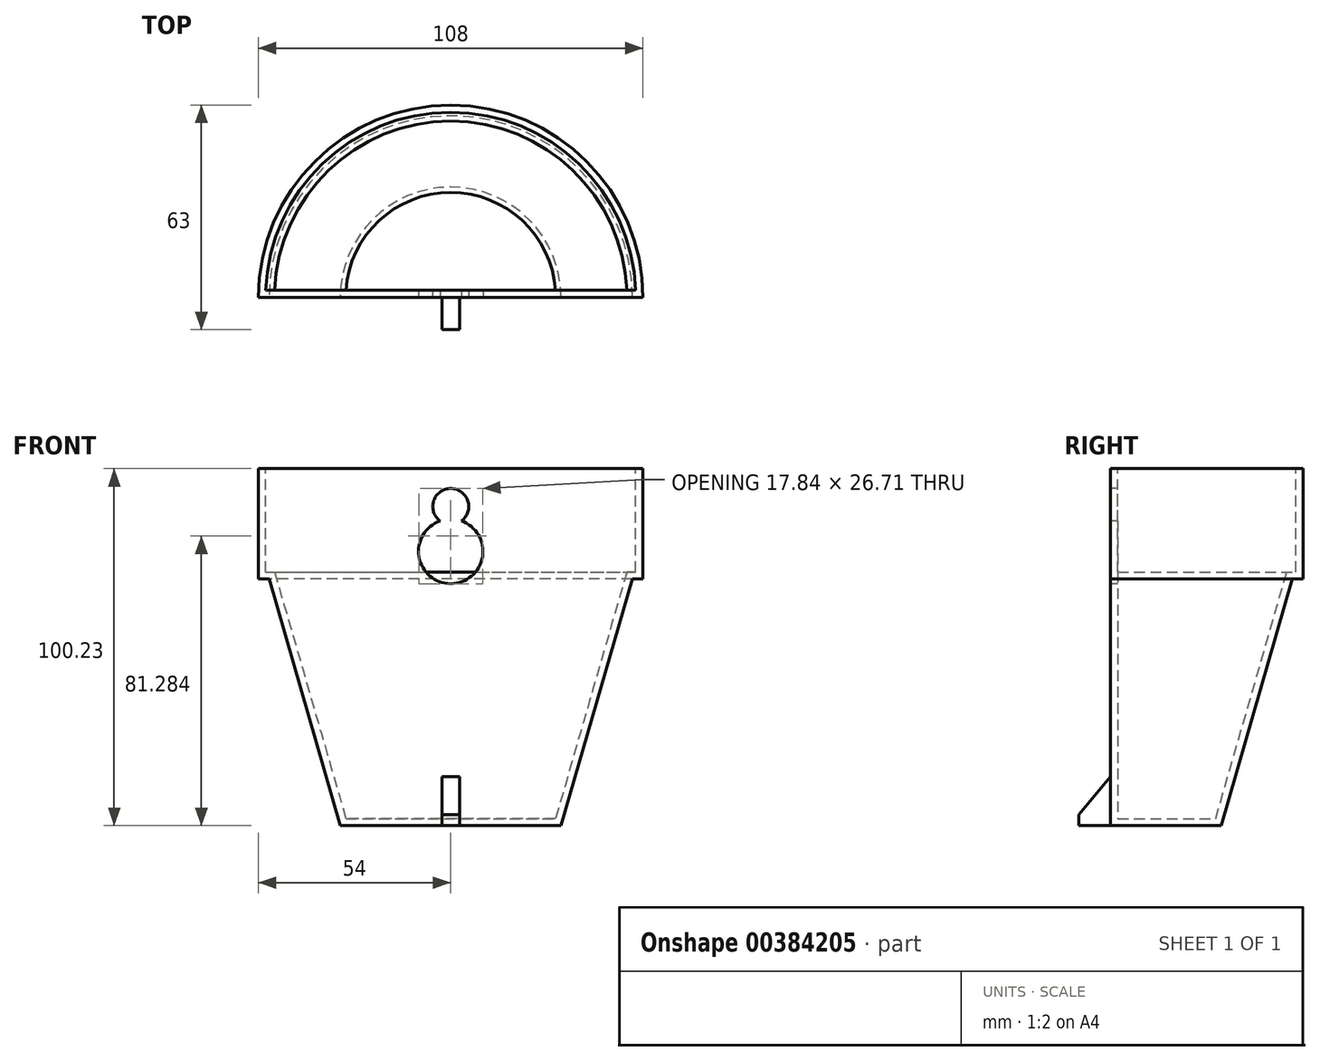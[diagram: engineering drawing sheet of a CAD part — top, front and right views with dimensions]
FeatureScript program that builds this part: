
annotation { "Feature Type Name" : "Feature", "Feature Type Description" : "" }
export const myFeature = defineFeature(function(context is Context, id is Id, definition is map)
    precondition{}
    {
        {
            var Q0;
            Q0=qCreatedBy(makeId("Front.planeOp"),FACE);
            var sketch = newSketch(context, id + "F0", { "sketchPlane" : qUnion([Q0])});
            skLineSegment(sketch, "E0", {"start": v(0, 49.42) * mm, "end": v(-54, 49.42) * mm});
            skLineSegment(sketch, "E1", {"start": v(-54, 49.42) * mm, "end": v(-54, 18.42) * mm});
            skLineSegment(sketch, "E2", {"start": v(0, -50.8) * mm, "end": v(-31, -50.8) * mm});
            skLineSegment(sketch, "E3", {"start": v(-54, 18.42) * mm, "end": v(-51, 18.42) * mm});
            skLineSegment(sketch, "E4", {"start": v(0, 49.42) * mm, "end": v(0, -50.8) * mm});
            skLineSegment(sketch, "E5", {"start": v(-51, 18.42) * mm, "end": v(-31, -50.8) * mm});
            skLineSegment(sketch, "E6.MirrorCS", {"start": v(0, 49.42) * mm, "end": v(54, 49.42) * mm});
            skLineSegment(sketch, "E7.MirrorCS", {"start": v(54, 49.42) * mm, "end": v(54, 18.42) * mm});
            skLineSegment(sketch, "E8.MirrorCS", {"start": v(54, 18.42) * mm, "end": v(51, 18.42) * mm});
            skLineSegment(sketch, "E9.MirrorCS", {"start": v(51, 18.42) * mm, "end": v(31, -50.8) * mm});
            skLineSegment(sketch, "E10.MirrorCS", {"start": v(0, -50.8) * mm, "end": v(31, -50.8) * mm});
            skSolve(sketch);
        }
        {
            var Q0;
            {var subQ0=sQuery(id+"F0.wireOp",EDGE,"E3");Q0=makeQuery(id+"F0.imprint","IMPRINT",FACE,{"disambiguationData":[TD([[makeQuery(id+"F0.imprint","IMPRINT",EDGE,{"derivedFrom":subQ0}),1.0]])]});}
            var Q1;
            {var subQ1=sQuery(id+"F0.wireOp",EDGE,"E0");Q1=makeQuery(id+"F0.imprint","IMPRINT",FACE,{"disambiguationData":[TD([[makeQuery(id+"F0.imprint","IMPRINT",EDGE,{"derivedFrom":subQ1}),1.0]])]});}
            var Q2;
            Q2=makeQuery(id+"F0.imprint","IMPRINT",FACE,{"disambiguationData":[TD([[makeQuery(id+"F0.imprint","IMPRINT",EDGE,{"derivedFrom":sQuery(id+"F0.wireOp",EDGE,"Kfnrekvc-ZjTY-c2iQ-cK4z-hKnBe4uEAVNk")}),1.0]])]});
            var Q3;
            Q3=sQuery(id+"F0.wireOp",EDGE,"E4");
            revolve(context, id + "F1", {"entities" : qUnion([Q0, Q1, Q2]), "axis" : qUnion([Q3]), "revolveType" : RevolveType.ONE_DIRECTION, "angle" : 180 * degree});
        }
        {
            var Q0;
            Q0=makeQuery(id+"FK2OT3XlAi37Aaq_1.splitOp","SPLIT",FACE,{"derivedFrom":makeQuery(id+"F1.opRevolve","SWEPT_FACE",FACE,{"disambiguationData":[OSD([sQuery(id+"F0.wireOp",EDGE,"E0")])]}),"isFromBackBody":true});
            shell(context, id + "F2", {"entities" : qUnion([Q0]), "thickness" : 2 * mm});
        }
        {
            var Q0;
            Q0=qCreatedBy(makeId("Front.planeOp"),FACE);
            var sketch = newSketch(context, id + "F3", { "sketchPlane" : qUnion([Q0])});
            skLineSegment(sketch, "E11.bottom", {"start": v(-2.5, -35.8) * mm, "end": v(2.5, -35.8) * mm});
            skLineSegment(sketch, "E11.top", {"start": v(-2.5, -50.8) * mm, "end": v(2.5, -50.8) * mm});
            skLineSegment(sketch, "E11.left", {"start": v(-2.5, -35.8) * mm, "end": v(-2.5, -50.8) * mm});
            skLineSegment(sketch, "E11.right", {"start": v(2.5, -35.8) * mm, "end": v(2.5, -50.8) * mm});
            skPoint(sketch, "E11.middle", {"position": v(0, -43.3) * mm});
            skSolve(sketch);
        }
        {
            var Q0;
            Q0 = qSketchRegion(id + "F3", true);
            extrude(context, id + "F4", {"entities" : qUnion([Q0]), "operationType" : NewBodyOperationType.ADD, "depth" : 9 * mm});
        }
        {
            var Q0;
            Q0=qCreatedBy(makeId("Front.planeOp"),FACE);
            var sketch = newSketch(context, id + "F5", { "sketchPlane" : qUnion([Q0])});
            skCircle(sketch, "E12", {"center": v(0, 38.78) * mm, "radius": 5.05 * mm});
            skCircle(sketch, "E13", {"center": v(0, 26.17) * mm, "radius": 9.05 * mm});
            skSolve(sketch);
        }
        {
            var Q0;
            {var subQ0=sQuery(id+"F5.wireOp",EDGE,"E13");var subQ1=sQuery(id+"F5.wireOp",EDGE,"E12");var subQ2=makeQuery(id+"F5.imprint","INTERSECT",VERTEX,{"disambiguationData":[OD(0.0)],"derivedFrom":[subQ1,subQ0]});Q0=makeQuery(id+"F5.imprint","IMPRINT",FACE,{"disambiguationData":[TD([[makeQuery(id+"F5.imprint","IMPRINT",EDGE,{"disambiguationData":[TD([[subQ2,1.0]])],"derivedFrom":subQ1}),1.0]])]});}
            var Q1;
            {var subQ0=sQuery(id+"F5.wireOp",EDGE,"E13");var subQ1=sQuery(id+"F5.wireOp",EDGE,"E12");var subQ2=makeQuery(id+"F5.imprint","INTERSECT",VERTEX,{"disambiguationData":[OD(0.0)],"derivedFrom":[subQ1,subQ0]});Q1=makeQuery(id+"F5.imprint","IMPRINT",FACE,{"disambiguationData":[TD([[makeQuery(id+"F5.imprint","IMPRINT",EDGE,{"disambiguationData":[TD([[subQ2,-1.0]])],"derivedFrom":subQ1}),-1.0]])]});}
            var Q2;
            {var subQ0=sQuery(id+"F5.wireOp",EDGE,"E13");var subQ1=sQuery(id+"F5.wireOp",EDGE,"E12");var subQ2=makeQuery(id+"F5.imprint","INTERSECT",VERTEX,{"disambiguationData":[OD(0.0)],"derivedFrom":[subQ1,subQ0]});Q2=makeQuery(id+"F5.imprint","IMPRINT",FACE,{"disambiguationData":[TD([[makeQuery(id+"F5.imprint","IMPRINT",EDGE,{"disambiguationData":[TD([[subQ2,-1.0]])],"derivedFrom":subQ1}),1.0]])]});}
            var Q3;
            Q3=sQuery(id+"F5.wireOp",EDGE,"E12");
            var Q4;
            Q4=sQuery(id+"F5.wireOp",EDGE,"E13");
            extrude(context, id + "F6", {"entities" : qUnion([Q0, Q1, Q2]), "operationType" : NewBodyOperationType.REMOVE, "surfaceEntities" : qUnion([Q3, Q4]), "oppositeDirection" : true, "depth" : 10 * mm});
        }
        {
            var Q0;
            Q0=makeQuery(id+"F4.opExtrude","CAP_EDGE",EDGE,{"disambiguationData":[OSD([sQuery(id+"F3.wireOp",EDGE,"E11.bottom")])],"isStart":false});
            chamfer(context, id + "F7", {"entities" : qUnion([Q0]), "chamferType" : ChamferType.OFFSET_ANGLE, "width" : 10 * mm, "oppositeDirection" : false, "angle" : 50 * degree, "tangentPropagation" : true});
        }
    });
